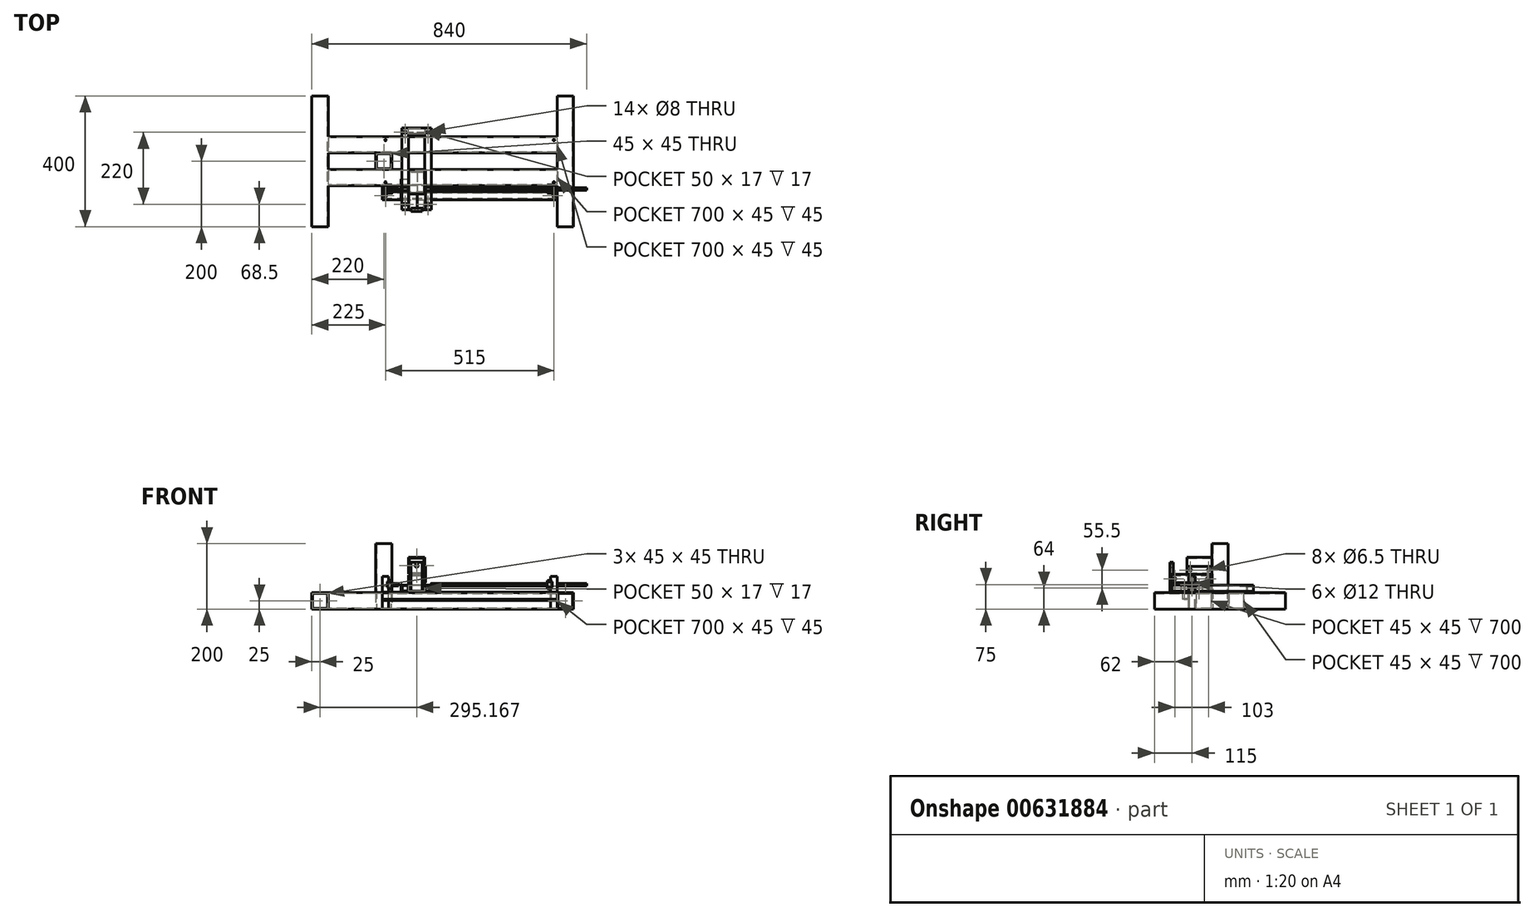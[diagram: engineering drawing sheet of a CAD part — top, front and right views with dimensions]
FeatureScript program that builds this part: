
annotation { "Feature Type Name" : "Feature", "Feature Type Description" : "" }
export const myFeature = defineFeature(function(context is Context, id is Id, definition is map)
    precondition{}
    {
        {
            var Q0;
            Q0=qCreatedBy(makeId("Front.planeOp"),FACE);
            var sketch = newSketch(context, id + "F0", { "sketchPlane" : qUnion([Q0])});
            skLineSegment(sketch, "E0.bottom", {"start": v(-400, -25) * mm, "end": v(-350, -25) * mm});
            skLineSegment(sketch, "E0.top", {"start": v(-400, 25) * mm, "end": v(-350, 25) * mm});
            skLineSegment(sketch, "E0.left", {"start": v(-400, -25) * mm, "end": v(-400, 25) * mm});
            skLineSegment(sketch, "E0.right", {"start": v(-350, -25) * mm, "end": v(-350, 25) * mm});
            skPoint(sketch, "E0.middle", {"position": v(-375, 0) * mm});
            skLineSegment(sketch, "E1.bottom", {"start": v(350, -25) * mm, "end": v(400, -25) * mm});
            skLineSegment(sketch, "E1.top", {"start": v(350, 25) * mm, "end": v(400, 25) * mm});
            skLineSegment(sketch, "E1.left", {"start": v(350, -25) * mm, "end": v(350, 25) * mm});
            skLineSegment(sketch, "E1.right", {"start": v(400, -25) * mm, "end": v(400, 25) * mm});
            skPoint(sketch, "E1.middle", {"position": v(375, 0) * mm});
            skLineSegment(sketch, "E2.bottom", {"start": v(-397.5, -22.5) * mm, "end": v(-352.5, -22.5) * mm});
            skLineSegment(sketch, "E2.top", {"start": v(-397.5, 22.5) * mm, "end": v(-352.5, 22.5) * mm});
            skLineSegment(sketch, "E2.left", {"start": v(-397.5, -22.5) * mm, "end": v(-397.5, 22.5) * mm});
            skLineSegment(sketch, "E2.right", {"start": v(-352.5, -22.5) * mm, "end": v(-352.5, 22.5) * mm});
            skLineSegment(sketch, "E3.bottom", {"start": v(352.5, -22.5) * mm, "end": v(397.5, -22.5) * mm});
            skLineSegment(sketch, "E3.top", {"start": v(352.5, 22.5) * mm, "end": v(397.5, 22.5) * mm});
            skLineSegment(sketch, "E3.left", {"start": v(352.5, -22.5) * mm, "end": v(352.5, 22.5) * mm});
            skLineSegment(sketch, "E3.right", {"start": v(397.5, -22.5) * mm, "end": v(397.5, 22.5) * mm});
            skSolve(sketch);
        }
        {
            var Q0;
            Q0=qSketchRegion(id+"F0",true);
            extrude(context, id + "F1", {"entities" : qUnion([Q0]), "endBound" : BoundingType.SYMMETRIC, "depth" : 400 * mm, "offsetDistance" : 25 * mm});
        }
        {
            var Q0;
            Q0=makeQuery(id+"F1.opExtrude","SWEPT_FACE",FACE,{"disambiguationData":[OSD([sQuery(id+"F0.wireOp",EDGE,"E0.right")])]});
            var sketch = newSketch(context, id + "F2", { "sketchPlane" : qUnion([Q0])});
            skPoint(sketch, "E4.middle", {"position": v(0, 0) * mm});
            skLineSegment(sketch, "E5.bottom", {"start": v(75, -25) * mm, "end": v(25, -25) * mm});
            skLineSegment(sketch, "E5.top", {"start": v(75, 25) * mm, "end": v(25, 25) * mm});
            skLineSegment(sketch, "E5.left", {"start": v(75, -25) * mm, "end": v(75, 25) * mm});
            skLineSegment(sketch, "E5.right", {"start": v(25, -25) * mm, "end": v(25, 25) * mm});
            skPoint(sketch, "E5.middle", {"position": v(50, 0) * mm});
            skLineSegment(sketch, "E6.bottom", {"start": v(-25, -25) * mm, "end": v(-75, -25) * mm});
            skLineSegment(sketch, "E6.top", {"start": v(-25, 25) * mm, "end": v(-75, 25) * mm});
            skLineSegment(sketch, "E6.left", {"start": v(-25, -25) * mm, "end": v(-25, 25) * mm});
            skLineSegment(sketch, "E6.right", {"start": v(-75, -25) * mm, "end": v(-75, 25) * mm});
            skPoint(sketch, "E6.middle", {"position": v(-50, 0) * mm});
            skLineSegment(sketch, "E7.bottom", {"start": v(72.5, 22.5) * mm, "end": v(27.5, 22.5) * mm});
            skLineSegment(sketch, "E7.top", {"start": v(72.5, -22.5) * mm, "end": v(27.5, -22.5) * mm});
            skLineSegment(sketch, "E7.left", {"start": v(72.5, 22.5) * mm, "end": v(72.5, -22.5) * mm});
            skLineSegment(sketch, "E7.right", {"start": v(27.5, 22.5) * mm, "end": v(27.5, -22.5) * mm});
            skLineSegment(sketch, "E8.bottom", {"start": v(-27.5, 22.5) * mm, "end": v(-72.5, 22.5) * mm});
            skLineSegment(sketch, "E8.top", {"start": v(-27.5, -22.5) * mm, "end": v(-72.5, -22.5) * mm});
            skLineSegment(sketch, "E8.left", {"start": v(-27.5, 22.5) * mm, "end": v(-27.5, -22.5) * mm});
            skLineSegment(sketch, "E8.right", {"start": v(-72.5, 22.5) * mm, "end": v(-72.5, -22.5) * mm});
            skSolve(sketch);
        }
        {
            var Q0;
            Q0=qSketchRegion(id+"F2",true);
            extrude(context, id + "F3", {"entities" : qUnion([Q0]), "operationType" : NewBodyOperationType.ADD, "endBound" : BoundingType.UP_TO_NEXT, "depth" : 25 * mm, "offsetDistance" : 25 * mm});
        }
        {
            var Q0;
            Q0=makeQuery(id+"F3.boolean.opBoolean","MERGE",FACE,{"derivedFrom":[makeQuery(id+"F1.opExtrude","SWEPT_FACE",FACE,{"disambiguationData":[OSD([sQuery(id+"F0.wireOp",EDGE,"E0.top")])]}),makeQuery(id+"F1.opExtrude","SWEPT_FACE",FACE,{"disambiguationData":[OSD([sQuery(id+"F0.wireOp",EDGE,"E1.top")])]}),makeQuery(id+"F3.opExtrude","SWEPT_FACE",FACE,{"disambiguationData":[OSD([sQuery(id+"F2.wireOp",EDGE,"E5.top")])]}),makeQuery(id+"F3.opExtrude","SWEPT_FACE",FACE,{"disambiguationData":[OSD([sQuery(id+"F2.wireOp",EDGE,"E6.top")])]})]});
            var sketch = newSketch(context, id + "F4", { "sketchPlane" : qUnion([Q0])});
            skLineSegment(sketch, "E9.bottom", {"start": v(350, -75) * mm, "end": v(330, -75) * mm});
            skLineSegment(sketch, "E9.top", {"start": v(350, -95) * mm, "end": v(330, -95) * mm});
            skLineSegment(sketch, "E9.left", {"start": v(350, -75) * mm, "end": v(350, -95) * mm});
            skLineSegment(sketch, "E9.right", {"start": v(330, -75) * mm, "end": v(330, -95) * mm});
            skLineSegment(sketch, "E10.bottom", {"start": v(-165, -75) * mm, "end": v(-185, -75) * mm});
            skLineSegment(sketch, "E10.top", {"start": v(-165, -95) * mm, "end": v(-185, -95) * mm});
            skLineSegment(sketch, "E10.left", {"start": v(-165, -75) * mm, "end": v(-165, -95) * mm});
            skLineSegment(sketch, "E10.right", {"start": v(-185, -75) * mm, "end": v(-185, -95) * mm});
            skLineSegment(sketch, "E11.bottom", {"start": v(-183.5, -93.5) * mm, "end": v(-166.5, -93.5) * mm});
            skLineSegment(sketch, "E11.top", {"start": v(-183.5, -76.5) * mm, "end": v(-166.5, -76.5) * mm});
            skLineSegment(sketch, "E11.left", {"start": v(-183.5, -93.5) * mm, "end": v(-183.5, -76.5) * mm});
            skLineSegment(sketch, "E11.right", {"start": v(-166.5, -93.5) * mm, "end": v(-166.5, -76.5) * mm});
            skPoint(sketch, "E11.middle", {"position": v(-175, -85) * mm});
            skPoint(sketch, "E11.middle.positionSnap0", {"position": v(-165, -85) * mm});
            skPoint(sketch, "E11.middle.positionSnap1", {"position": v(-175, -95) * mm});
            skPoint(sketch, "E11.centerSnap0", {"position": v(-165, -85) * mm});
            skPoint(sketch, "E11.centerSnap1", {"position": v(-175, -95) * mm});
            skLineSegment(sketch, "E12.bottom", {"start": v(331.5, -93.5) * mm, "end": v(348.5, -93.5) * mm});
            skLineSegment(sketch, "E12.top", {"start": v(331.5, -76.5) * mm, "end": v(348.5, -76.5) * mm});
            skLineSegment(sketch, "E12.left", {"start": v(331.5, -93.5) * mm, "end": v(331.5, -76.5) * mm});
            skLineSegment(sketch, "E12.right", {"start": v(348.5, -93.5) * mm, "end": v(348.5, -76.5) * mm});
            skPoint(sketch, "E12.middle", {"position": v(340, -85) * mm});
            skPoint(sketch, "E12.middle.positionSnap0", {"position": v(330, -85) * mm});
            skPoint(sketch, "E12.middle.positionSnap1", {"position": v(340, -75) * mm});
            skPoint(sketch, "E12.centerSnap0", {"position": v(330, -85) * mm});
            skPoint(sketch, "E12.centerSnap1", {"position": v(340, -75) * mm});
            skSolve(sketch);
        }
        {
            var Q0;
            Q0=qSketchRegion(id+"F4",true);
            extrude(context, id + "F5", {"entities" : qUnion([Q0]), "operationType" : NewBodyOperationType.ADD, "oppositeDirection" : true, "depth" : 50 * mm, "offsetDistance" : 25 * mm});
        }
        {
            var Q0;
            Q0=qSketchRegion(id+"F4",true);
            extrude(context, id + "F6", {"entities" : qUnion([Q0]), "operationType" : NewBodyOperationType.ADD, "depth" : 50 * mm, "offsetDistance" : 25 * mm});
        }
        {
            var Q0;
            {var subQ1=sQuery(id+"F0.wireOp",EDGE,"E1.left");Q0=makeQuery(id+"F3.boolean.opBoolean","SPLIT",FACE,{"disambiguationData":[TD([makeQuery(id+"F3.opExtrude","SWEPT_FACE",FACE,{"disambiguationData":[OSD([sQuery(id+"F2.wireOp",EDGE,"E6.right")])]})])],"derivedFrom":makeQuery(id+"F1.opExtrude","SWEPT_FACE",FACE,{"disambiguationData":[OSD([subQ1])]})});}
            var sketch = newSketch(context, id + "F7", { "sketchPlane" : qUnion([Q0])});
            skLineSegment(sketch, "E13.bottom", {"start": v(95, 25) * mm, "end": v(115, 25) * mm});
            skLineSegment(sketch, "E13.top", {"start": v(95, 5) * mm, "end": v(115, 5) * mm});
            skLineSegment(sketch, "E13.left", {"start": v(95, 25) * mm, "end": v(95, 5) * mm});
            skLineSegment(sketch, "E13.right", {"start": v(115, 25) * mm, "end": v(115, 5) * mm});
            skPoint(sketch, "E13.middle", {"position": v(105, 15) * mm});
            skLineSegment(sketch, "E14.bottom", {"start": v(96.5, 6.5) * mm, "end": v(113.5, 6.5) * mm});
            skLineSegment(sketch, "E14.top", {"start": v(96.5, 23.5) * mm, "end": v(113.5, 23.5) * mm});
            skLineSegment(sketch, "E14.left", {"start": v(96.5, 6.5) * mm, "end": v(96.5, 23.5) * mm});
            skLineSegment(sketch, "E14.right", {"start": v(113.5, 6.5) * mm, "end": v(113.5, 23.5) * mm});
            skSolve(sketch);
        }
        {
            var Q0;
            Q0=qSketchRegion(id+"F7",true);
            extrude(context, id + "F8", {"entities" : qUnion([Q0]), "operationType" : NewBodyOperationType.ADD, "depth" : 535 * mm, "offsetDistance" : 25 * mm});
        }
        {
            var Q0;
            Q0=makeQuery(id+"F6.opExtrude","SWEPT_FACE",FACE,{"disambiguationData":[OSD([sQuery(id+"F4.wireOp",EDGE,"E9.left")])]});
            var sketch = newSketch(context, id + "F9", { "sketchPlane" : qUnion([Q0])});
            skCircle(sketch, "E15", {"center": v(-85, 50) * mm, "radius": 6 * mm});
            skPoint(sketch, "E15.centerSnap0", {"position": v(-85, 75) * mm});
            skSolve(sketch);
        }
        {
            var Q0;
            Q0=qSketchRegion(id+"F9",true);
            extrude(context, id + "F10", {"entities" : qUnion([Q0]), "operationType" : NewBodyOperationType.REMOVE, "endBound" : BoundingType.THROUGH_ALL, "oppositeDirection" : true, "depth" : 242 * mm, "offsetDistance" : 25 * mm});
        }
        {
            var Q0;
            {var subQ0=sQuery(id+"F4.wireOp",EDGE,"E9.right");Q0=makeQuery(id+"F6.boolean.opBoolean","MERGE",FACE,{"derivedFrom":[makeQuery(id+"F5.opExtrude","SWEPT_FACE",FACE,{"disambiguationData":[OSD([subQ0])]}),makeQuery(id+"F6.opExtrude","SWEPT_FACE",FACE,{"disambiguationData":[OSD([subQ0])]})]});}
            var sketch = newSketch(context, id + "F11", { "sketchPlane" : qUnion([Q0])});
            skCircle(sketch, "E16", {"center": v(85, 50) * mm, "radius": 11 * mm});
            skCircle(sketch, "E17", {"center": v(85, 50) * mm, "radius": 13 * mm});
            skSolve(sketch);
        }
        {
            var Q0;
            Q0=qSketchRegion(id+"F11",true);
            extrude(context, id + "F12", {"entities" : qUnion([Q0]), "operationType" : NewBodyOperationType.ADD, "depth" : 10 * mm, "offsetDistance" : 25 * mm});
        }
        {
            var Q0;
            Q0=qSketchRegion(id+"F11",true);
            extrude(context, id + "F13", {"entities" : qUnion([Q0]), "operationType" : NewBodyOperationType.ADD, "oppositeDirection" : true, "depth" : 5 * mm, "offsetDistance" : 25 * mm});
        }
        {
            var Q0;
            {var subQ0=sQuery(id+"F4.wireOp",EDGE,"E10.left");Q0=makeQuery(id+"F6.boolean.opBoolean","MERGE",FACE,{"derivedFrom":[makeQuery(id+"F5.opExtrude","SWEPT_FACE",FACE,{"disambiguationData":[OSD([subQ0])]}),makeQuery(id+"F6.opExtrude","SWEPT_FACE",FACE,{"disambiguationData":[OSD([subQ0])]})]});}
            var sketch = newSketch(context, id + "F14", { "sketchPlane" : qUnion([Q0])});
            skCircle(sketch, "E18", {"center": v(-85, 50) * mm, "radius": 11 * mm});
            skCircle(sketch, "E19", {"center": v(-85, 50) * mm, "radius": 13 * mm});
            skSolve(sketch);
        }
        {
            var Q0;
            Q0=qSketchRegion(id+"F14",true);
            extrude(context, id + "F15", {"entities" : qUnion([Q0]), "operationType" : NewBodyOperationType.ADD, "depth" : 10 * mm, "offsetDistance" : 25 * mm});
        }
        {
            var Q0;
            Q0=qSketchRegion(id+"F14",true);
            extrude(context, id + "F16", {"entities" : qUnion([Q0]), "operationType" : NewBodyOperationType.ADD, "oppositeDirection" : true, "depth" : 5 * mm, "offsetDistance" : 25 * mm});
        }
        {
            var Q0;
            {var subQ0=sQuery(id+"F4.wireOp",EDGE,"E10.left");var subQ1=sQuery(id+"F14.wireOp",EDGE,"E19");Q0=makeQuery(id+"F15.boolean.opBoolean","SPLIT",EDGE,{"disambiguationData":[topologyDisambiguationEdgeConnected([makeQuery(id+"F5.opExtrude","SWEPT_FACE",FACE,{"disambiguationData":[OSD([subQ0])]}),makeQuery(id+"F6.opExtrude","SWEPT_FACE",FACE,{"disambiguationData":[OSD([subQ0])]}),makeQuery(id+"F15.opExtrude","SWEPT_FACE",FACE,{"disambiguationData":[OSD([subQ1])]})]),OD(1.0)],"derivedFrom":makeQuery(id+"F15.opExtrude","CAP_EDGE",EDGE,{"disambiguationData":[OSD([subQ1])],"isStart":true})});}
            var Q1;
            {var subQ0=sQuery(id+"F4.wireOp",EDGE,"E10.left");var subQ1=sQuery(id+"F14.wireOp",EDGE,"E19");Q1=makeQuery(id+"F15.boolean.opBoolean","SPLIT",EDGE,{"disambiguationData":[topologyDisambiguationEdgeConnected([makeQuery(id+"F5.opExtrude","SWEPT_FACE",FACE,{"disambiguationData":[OSD([subQ0])]}),makeQuery(id+"F6.opExtrude","SWEPT_FACE",FACE,{"disambiguationData":[OSD([subQ0])]}),makeQuery(id+"F15.opExtrude","SWEPT_FACE",FACE,{"disambiguationData":[OSD([subQ1])]})]),OD(0.0)],"derivedFrom":makeQuery(id+"F15.opExtrude","CAP_EDGE",EDGE,{"disambiguationData":[OSD([subQ1])],"isStart":true})});}
            var Q2;
            {var subQ0=sQuery(id+"F4.wireOp",EDGE,"E9.right");var subQ1=sQuery(id+"F11.wireOp",EDGE,"E17");Q2=makeQuery(id+"F12.boolean.opBoolean","SPLIT",EDGE,{"disambiguationData":[topologyDisambiguationEdgeConnected([makeQuery(id+"F5.opExtrude","SWEPT_FACE",FACE,{"disambiguationData":[OSD([subQ0])]}),makeQuery(id+"F6.opExtrude","SWEPT_FACE",FACE,{"disambiguationData":[OSD([subQ0])]}),makeQuery(id+"F12.opExtrude","SWEPT_FACE",FACE,{"disambiguationData":[OSD([subQ1])]})]),OD(1.0)],"derivedFrom":makeQuery(id+"F12.opExtrude","CAP_EDGE",EDGE,{"disambiguationData":[OSD([subQ1])],"isStart":true})});}
            var Q3;
            {var subQ0=sQuery(id+"F4.wireOp",EDGE,"E9.right");var subQ1=sQuery(id+"F11.wireOp",EDGE,"E17");Q3=makeQuery(id+"F12.boolean.opBoolean","SPLIT",EDGE,{"disambiguationData":[topologyDisambiguationEdgeConnected([makeQuery(id+"F5.opExtrude","SWEPT_FACE",FACE,{"disambiguationData":[OSD([subQ0])]}),makeQuery(id+"F6.opExtrude","SWEPT_FACE",FACE,{"disambiguationData":[OSD([subQ0])]}),makeQuery(id+"F12.opExtrude","SWEPT_FACE",FACE,{"disambiguationData":[OSD([subQ1])]})]),OD(0.0)],"derivedFrom":makeQuery(id+"F12.opExtrude","CAP_EDGE",EDGE,{"disambiguationData":[OSD([subQ1])],"isStart":true})});}
            chamfer(context, id + "F17", {"entities" : qUnion([Q0, Q1, Q2, Q3]), "width" : 5 * mm, "tangentPropagation" : true});
        }
        {
            var Q0;
            Q0=makeQuery(id+"F8.boolean.opBoolean","MERGE",FACE,{"derivedFrom":[makeQuery(id+"F5.boolean.opBoolean","MERGE",FACE,{"derivedFrom":[makeQuery(id+"F3.boolean.opBoolean","MERGE",FACE,{"derivedFrom":[makeQuery(id+"F1.opExtrude","SWEPT_FACE",FACE,{"disambiguationData":[OSD([sQuery(id+"F0.wireOp",EDGE,"E0.top")])]}),makeQuery(id+"F1.opExtrude","SWEPT_FACE",FACE,{"disambiguationData":[OSD([sQuery(id+"F0.wireOp",EDGE,"E1.top")])]}),makeQuery(id+"F3.opExtrude","SWEPT_FACE",FACE,{"disambiguationData":[OSD([sQuery(id+"F2.wireOp",EDGE,"E5.top")])]}),makeQuery(id+"F3.opExtrude","SWEPT_FACE",FACE,{"disambiguationData":[OSD([sQuery(id+"F2.wireOp",EDGE,"E6.top")])]})]}),makeQuery(id+"F5.opExtrude","CAP_FACE",FACE,{"disambiguationData":[OSD([sQuery(id+"F4.wireOp",EDGE,"E9.bottom"),sQuery(id+"F4.wireOp",EDGE,"E9.top"),sQuery(id+"F4.wireOp",EDGE,"E9.left"),sQuery(id+"F4.wireOp",EDGE,"E9.right"),sQuery(id+"F4.wireOp",EDGE,"E12.bottom"),sQuery(id+"F4.wireOp",EDGE,"E12.top"),sQuery(id+"F4.wireOp",EDGE,"E12.left"),sQuery(id+"F4.wireOp",EDGE,"E12.right")])],"isStart":true}),makeQuery(id+"F5.opExtrude","CAP_FACE",FACE,{"disambiguationData":[OSD([sQuery(id+"F4.wireOp",EDGE,"E10.bottom"),sQuery(id+"F4.wireOp",EDGE,"E10.top"),sQuery(id+"F4.wireOp",EDGE,"E10.left"),sQuery(id+"F4.wireOp",EDGE,"E10.right"),sQuery(id+"F4.wireOp",EDGE,"E11.bottom"),sQuery(id+"F4.wireOp",EDGE,"E11.top"),sQuery(id+"F4.wireOp",EDGE,"E11.left"),sQuery(id+"F4.wireOp",EDGE,"E11.right")])],"isStart":true})]}),makeQuery(id+"F8.opExtrude","SWEPT_FACE",FACE,{"disambiguationData":[OSD([sQuery(id+"F7.wireOp",EDGE,"E13.bottom")])]})]});
            var sketch = newSketch(context, id + "F18", { "sketchPlane" : qUnion([Q0])});
            skCircle(sketch, "E20", {"center": v(-175, -65) * mm, "radius": 2.5 * mm});
            skCircle(sketch, "E21", {"center": v(-175, 65) * mm, "radius": 2.5 * mm});
            skCircle(sketch, "E22", {"center": v(-175, -105) * mm, "radius": 2.5 * mm});
            skCircle(sketch, "E23", {"center": v(340, -105) * mm, "radius": 2.5 * mm});
            skCircle(sketch, "E24", {"center": v(340, -65) * mm, "radius": 2.5 * mm});
            skCircle(sketch, "E25", {"center": v(340, 65) * mm, "radius": 2.5 * mm});
            skSolve(sketch);
        }
        {
            var Q0;
            Q0=qSketchRegion(id+"F18",true);
            extrude(context, id + "F19", {"entities" : qUnion([Q0]), "operationType" : NewBodyOperationType.REMOVE, "oppositeDirection" : true, "depth" : 10 * mm, "offsetDistance" : 25 * mm});
        }
        {
            var Q0;
            Q0=makeQuery(id+"F6.opExtrude","SWEPT_FACE",FACE,{"disambiguationData":[OSD([sQuery(id+"F4.wireOp",EDGE,"E9.left")])]});
            var sketch = newSketch(context, id + "F20", { "sketchPlane" : qUnion([Q0])});
            skLineSegment(sketch, "E26", {"start": v(-118, 25) * mm, "end": v(-95, 25) * mm});
            skLineSegment(sketch, "E27", {"start": v(-95, 25) * mm, "end": v(-95, 2) * mm});
            skLineSegment(sketch, "E28", {"start": v(-95, 2) * mm, "end": v(-93, 2) * mm});
            skLineSegment(sketch, "E29", {"start": v(-93, 2) * mm, "end": v(-93, 27) * mm});
            skLineSegment(sketch, "E30", {"start": v(-93, 27) * mm, "end": v(-118, 27) * mm});
            skLineSegment(sketch, "E31", {"start": v(-118, 27) * mm, "end": v(-118, 25) * mm});
            skSolve(sketch);
        }
        {
            var Q0;
            Q0 = qSketchRegion(id + "F20", true);
            extrude(context, id + "F21", {"entities" : qUnion([Q0]), "oppositeDirection" : true, "depth" : 535 * mm, "offsetDistance" : 25 * mm});
        }
        {
            var Q0;
            Q0=makeQuery(id+"F21.opExtrude","SWEPT_FACE",FACE,{"disambiguationData":[OSD([sQuery(id+"F20.wireOp",EDGE,"E30")])]});
            var sketch = newSketch(context, id + "F22", { "sketchPlane" : qUnion([Q0])});
            skLineSegment(sketch, "E32.bottom", {"start": v(-185, -93) * mm, "end": v(-165, -93) * mm});
            skLineSegment(sketch, "E32.top", {"start": v(-185, -95) * mm, "end": v(-165, -95) * mm});
            skLineSegment(sketch, "E32.left", {"start": v(-185, -93) * mm, "end": v(-185, -95) * mm});
            skLineSegment(sketch, "E32.right", {"start": v(-165, -93) * mm, "end": v(-165, -95) * mm});
            skLineSegment(sketch, "E33.bottom", {"start": v(350, -93) * mm, "end": v(330, -93) * mm});
            skLineSegment(sketch, "E33.top", {"start": v(350, -95) * mm, "end": v(330, -95) * mm});
            skLineSegment(sketch, "E33.left", {"start": v(350, -93) * mm, "end": v(350, -95) * mm});
            skLineSegment(sketch, "E33.right", {"start": v(330, -93) * mm, "end": v(330, -95) * mm});
            skCircle(sketch, "E34", {"center": v(-175, -105) * mm, "radius": 4 * mm});
            skCircle(sketch, "E35", {"center": v(340, -105) * mm, "radius": 4 * mm});
            skSolve(sketch);
        }
        {
            var Q0;
            Q0 = qSketchRegion(id + "F22", true);
            extrude(context, id + "F23", {"entities" : qUnion([Q0]), "operationType" : NewBodyOperationType.REMOVE, "oppositeDirection" : true, "depth" : 26 * mm, "offsetDistance" : 25 * mm});
        }
        {
            var Q0;
            Q0=makeQuery(id+"F6.opExtrude","SWEPT_FACE",FACE,{"disambiguationData":[OSD([sQuery(id+"F4.wireOp",EDGE,"E9.left")])]});
            var sketch = newSketch(context, id + "F24", { "sketchPlane" : qUnion([Q0])});
            skCircle(sketch, "E36", {"center": v(-85, 50) * mm, "radius": 3.8 * mm});
            skSolve(sketch);
        }
        {
            var Q0;
            Q0 = qSketchRegion(id + "F24", true);
            extrude(context, id + "F25", {"entities" : qUnion([Q0]), "oppositeDirection" : true, "depth" : 535 * mm, "offsetDistance" : 25 * mm, "hasSecondDirection" : true, "secondDirectionOppositeDirection" : false, "secondDirectionDepth" : 90 * mm});
        }
        {
            var Q0;
            Q0=makeQuery(id+"F21.opExtrude","SWEPT_FACE",FACE,{"disambiguationData":[OSD([sQuery(id+"F20.wireOp",EDGE,"E31")])]});
            var sketch = newSketch(context, id + "F26", { "sketchPlane" : qUnion([Q0])});
            skLineSegment(sketch, "E37", {"start": v(-126.83, 27) * mm, "end": v(-126.83, 52) * mm});
            skLineSegment(sketch, "E38", {"start": v(-126.83, 52) * mm, "end": v(-124.83, 52) * mm});
            skLineSegment(sketch, "E39", {"start": v(-124.83, 52) * mm, "end": v(-124.83, 29) * mm});
            skLineSegment(sketch, "E40", {"start": v(-124.83, 29) * mm, "end": v(-101.83, 29) * mm});
            skLineSegment(sketch, "E41", {"start": v(-101.83, 29) * mm, "end": v(-101.83, 27) * mm});
            skLineSegment(sketch, "E42", {"start": v(-101.83, 27) * mm, "end": v(-126.83, 27) * mm});
            skSolve(sketch);
        }
        {
            var Q0;
            Q0 = qSketchRegion(id + "F26", true);
            extrude(context, id + "F27", {"entities" : qUnion([Q0]), "oppositeDirection" : true, "depth" : 64 * mm, "offsetDistance" : 25 * mm});
        }
        {
            var Q0;
            Q0=makeQuery(id+"F27.opExtrude","SWEPT_FACE",FACE,{"disambiguationData":[OSD([sQuery(id+"F26.wireOp",EDGE,"E37")])]});
            var sketch = newSketch(context, id + "F28", { "sketchPlane" : qUnion([Q0])});
            skArc(sketch, "E43", {"start": v(79, 50) * mm, "mid": v(85, 44) * mm, "end": v(91, 50) * mm});
            skLineSegment(sketch, "E44", {"start": v(79, 50) * mm, "end": v(79, 58) * mm});
            skLineSegment(sketch, "E45", {"start": v(79, 58) * mm, "end": v(91, 58) * mm});
            skLineSegment(sketch, "E46", {"start": v(91, 58) * mm, "end": v(91, 50) * mm});
            skCircle(sketch, "E47", {"center": v(64, 39) * mm, "radius": 3.25 * mm});
            skCircle(sketch, "E48", {"center": v(108, 39) * mm, "radius": 3.25 * mm});
            skSolve(sketch);
        }
        {
            var Q0;
            Q0 = qSketchRegion(id + "F28", true);
            extrude(context, id + "F29", {"entities" : qUnion([Q0]), "operationType" : NewBodyOperationType.REMOVE, "oppositeDirection" : true, "depth" : 60.5 * mm, "offsetDistance" : 25 * mm});
        }
        {
            var Q0;
            Q0=makeQuery(id+"F27.opExtrude","CAP_FACE",FACE,{"disambiguationData":[OSD([sQuery(id+"F26.wireOp",EDGE,"E37"),sQuery(id+"F26.wireOp",EDGE,"E38"),sQuery(id+"F26.wireOp",EDGE,"E39"),sQuery(id+"F26.wireOp",EDGE,"E40"),sQuery(id+"F26.wireOp",EDGE,"E41"),sQuery(id+"F26.wireOp",EDGE,"E42")])],"isStart":true});
            var sketch = newSketch(context, id + "F30", { "sketchPlane" : qUnion([Q0])});
            skLineSegment(sketch, "E49.bottom", {"start": v(-124.83, 29) * mm, "end": v(-104.83, 29) * mm});
            skLineSegment(sketch, "E49.top", {"start": v(-124.83, 49) * mm, "end": v(-104.83, 49) * mm});
            skLineSegment(sketch, "E49.left", {"start": v(-124.83, 29) * mm, "end": v(-124.83, 49) * mm});
            skLineSegment(sketch, "E49.right", {"start": v(-104.83, 29) * mm, "end": v(-104.83, 49) * mm});
            skLineSegment(sketch, "E50.bottom", {"start": v(-104.83, 29) * mm, "end": v(-54.83, 29) * mm});
            skLineSegment(sketch, "E50.top", {"start": v(-104.83, 79) * mm, "end": v(-54.83, 79) * mm});
            skLineSegment(sketch, "E50.left", {"start": v(-104.83, 29) * mm, "end": v(-104.83, 79) * mm});
            skLineSegment(sketch, "E50.right", {"start": v(-54.83, 29) * mm, "end": v(-54.83, 79) * mm});
            skLineSegment(sketch, "E51.bottom", {"start": v(-54.83, 29) * mm, "end": v(-34.83, 29) * mm});
            skLineSegment(sketch, "E51.top", {"start": v(-54.83, 49) * mm, "end": v(-34.83, 49) * mm});
            skLineSegment(sketch, "E51.left", {"start": v(-54.83, 29) * mm, "end": v(-54.83, 49) * mm});
            skLineSegment(sketch, "E51.right", {"start": v(-34.83, 29) * mm, "end": v(-34.83, 49) * mm});
            skLineSegment(sketch, "E52.bottom", {"start": v(-102.33, 31.5) * mm, "end": v(-57.33, 31.5) * mm});
            skLineSegment(sketch, "E52.top", {"start": v(-102.33, 76.5) * mm, "end": v(-57.33, 76.5) * mm});
            skLineSegment(sketch, "E52.left", {"start": v(-102.33, 31.5) * mm, "end": v(-102.33, 76.5) * mm});
            skLineSegment(sketch, "E52.right", {"start": v(-57.33, 31.5) * mm, "end": v(-57.33, 76.5) * mm});
            skPoint(sketch, "E52.middle", {"position": v(-79.83, 54) * mm});
            skPoint(sketch, "E52.middle.positionSnap0", {"position": v(-79.83, 79) * mm});
            skPoint(sketch, "E52.middle.positionSnap1", {"position": v(-104.83, 54) * mm});
            skPoint(sketch, "E52.centerSnap0", {"position": v(-79.83, 79) * mm});
            skPoint(sketch, "E52.centerSnap1", {"position": v(-104.83, 54) * mm});
            skLineSegment(sketch, "E53.bottom", {"start": v(-123.33, 30.5) * mm, "end": v(-106.33, 30.5) * mm});
            skLineSegment(sketch, "E53.top", {"start": v(-123.33, 47.5) * mm, "end": v(-106.33, 47.5) * mm});
            skLineSegment(sketch, "E53.left", {"start": v(-123.33, 30.5) * mm, "end": v(-123.33, 47.5) * mm});
            skLineSegment(sketch, "E53.right", {"start": v(-106.33, 30.5) * mm, "end": v(-106.33, 47.5) * mm});
            skPoint(sketch, "E53.middle", {"position": v(-114.83, 39) * mm});
            skPoint(sketch, "E53.middle.positionSnap0", {"position": v(-104.83, 39) * mm});
            skPoint(sketch, "E53.middle.positionSnap1", {"position": v(-114.83, 49) * mm});
            skPoint(sketch, "E53.centerSnap0", {"position": v(-104.83, 39) * mm});
            skPoint(sketch, "E53.centerSnap1", {"position": v(-114.83, 49) * mm});
            skLineSegment(sketch, "E54.bottom", {"start": v(-53.33, 30.5) * mm, "end": v(-36.33, 30.5) * mm});
            skLineSegment(sketch, "E54.top", {"start": v(-53.33, 47.5) * mm, "end": v(-36.33, 47.5) * mm});
            skLineSegment(sketch, "E54.left", {"start": v(-53.33, 30.5) * mm, "end": v(-53.33, 47.5) * mm});
            skLineSegment(sketch, "E54.right", {"start": v(-36.33, 30.5) * mm, "end": v(-36.33, 47.5) * mm});
            skPoint(sketch, "E54.middle", {"position": v(-44.83, 39) * mm});
            skPoint(sketch, "E54.middle.positionSnap0", {"position": v(-44.83, 49) * mm});
            skPoint(sketch, "E54.centerSnap0", {"position": v(-44.83, 49) * mm});
            skSolve(sketch);
        }
        {
            var Q0;
            Q0 = qSketchRegion(id + "F30", true);
            extrude(context, id + "F31", {"entities" : qUnion([Q0]), "oppositeDirection" : true, "depth" : 90 * mm, "offsetDistance" : 25 * mm, "hasSecondDirection" : true, "secondDirectionOppositeDirection" : false, "secondDirectionDepth" : 30 * mm});
        }
        {
            var Q0;
            Q0=makeQuery(id+"F31.opExtrude","SWEPT_FACE",FACE,{"disambiguationData":[OSD([sQuery(id+"F30.wireOp",EDGE,"E51.right")])]});
            var sketch = newSketch(context, id + "F32", { "sketchPlane" : qUnion([Q0])});
            skCircle(sketch, "E55", {"center": v(-85, 50) * mm, "radius": 6 * mm});
            skCircle(sketch, "E56", {"center": v(-138, 67.5) * mm, "radius": 3.25 * mm});
            skCircle(sketch, "E57", {"center": v(-38, 67.5) * mm, "radius": 3.25 * mm});
            skSolve(sketch);
        }
        {
            var Q0;
            Q0 = qSketchRegion(id + "F32", true);
            extrude(context, id + "F33", {"entities" : qUnion([Q0]), "operationType" : NewBodyOperationType.REMOVE, "oppositeDirection" : true, "depth" : 100.4 * mm, "offsetDistance" : 25 * mm});
        }
        {
            var Q0;
            Q0=makeQuery(id+"F31.opExtrude","CAP_FACE",FACE,{"disambiguationData":[OSD([sQuery(id+"F30.wireOp",EDGE,"E49.bottom"),sQuery(id+"F30.wireOp",EDGE,"E49.top"),sQuery(id+"F30.wireOp",EDGE,"E49.left"),sQuery(id+"F30.wireOp",EDGE,"E50.bottom"),sQuery(id+"F30.wireOp",EDGE,"E50.top"),sQuery(id+"F30.wireOp",EDGE,"E50.left"),sQuery(id+"F30.wireOp",EDGE,"E50.right"),sQuery(id+"F30.wireOp",EDGE,"E51.bottom"),sQuery(id+"F30.wireOp",EDGE,"E51.top"),sQuery(id+"F30.wireOp",EDGE,"E51.right"),sQuery(id+"F30.wireOp",EDGE,"E52.bottom"),sQuery(id+"F30.wireOp",EDGE,"E52.top"),sQuery(id+"F30.wireOp",EDGE,"E52.left"),sQuery(id+"F30.wireOp",EDGE,"E52.right"),sQuery(id+"F30.wireOp",EDGE,"E53.bottom"),sQuery(id+"F30.wireOp",EDGE,"E53.top"),sQuery(id+"F30.wireOp",EDGE,"E53.left"),sQuery(id+"F30.wireOp",EDGE,"E53.right"),sQuery(id+"F30.wireOp",EDGE,"E54.bottom"),sQuery(id+"F30.wireOp",EDGE,"E54.top"),sQuery(id+"F30.wireOp",EDGE,"E54.left"),sQuery(id+"F30.wireOp",EDGE,"E54.right")])],"isStart":false});
            var sketch = newSketch(context, id + "F34", { "sketchPlane" : qUnion([Q0])});
            skLineSegment(sketch, "E58.bottom", {"start": v(34.83, 49) * mm, "end": v(54.83, 49) * mm});
            skLineSegment(sketch, "E58.top", {"start": v(34.83, 29) * mm, "end": v(54.83, 29) * mm});
            skLineSegment(sketch, "E58.left", {"start": v(34.83, 49) * mm, "end": v(34.83, 29) * mm});
            skLineSegment(sketch, "E58.right", {"start": v(54.83, 49) * mm, "end": v(54.83, 29) * mm});
            skPoint(sketch, "E58.middle", {"position": v(44.83, 39) * mm});
            skPoint(sketch, "E58.middle.positionSnap0", {"position": v(44.83, 47.5) * mm});
            skPoint(sketch, "E58.middle.positionSnap1", {"position": v(36.33, 39) * mm});
            skPoint(sketch, "E58.centerSnap0", {"position": v(44.83, 47.5) * mm});
            skPoint(sketch, "E58.centerSnap1", {"position": v(36.33, 39) * mm});
            skLineSegment(sketch, "E59.bottom", {"start": v(104.83, 49) * mm, "end": v(124.83, 49) * mm});
            skLineSegment(sketch, "E59.top", {"start": v(104.83, 29) * mm, "end": v(124.83, 29) * mm});
            skLineSegment(sketch, "E59.left", {"start": v(104.83, 49) * mm, "end": v(104.83, 29) * mm});
            skLineSegment(sketch, "E59.right", {"start": v(124.83, 49) * mm, "end": v(124.83, 29) * mm});
            skPoint(sketch, "E59.middle", {"position": v(114.83, 39) * mm});
            skPoint(sketch, "E59.middle.positionSnap0", {"position": v(114.83, 47.5) * mm});
            skPoint(sketch, "E59.middle.positionSnap1", {"position": v(106.33, 39) * mm});
            skPoint(sketch, "E59.centerSnap0", {"position": v(114.83, 47.5) * mm});
            skPoint(sketch, "E59.centerSnap1", {"position": v(106.33, 39) * mm});
            skLineSegment(sketch, "E60.bottom", {"start": v(106.33, 47.5) * mm, "end": v(123.33, 47.5) * mm});
            skLineSegment(sketch, "E60.top", {"start": v(106.33, 30.5) * mm, "end": v(123.33, 30.5) * mm});
            skLineSegment(sketch, "E60.left", {"start": v(106.33, 47.5) * mm, "end": v(106.33, 30.5) * mm});
            skLineSegment(sketch, "E60.right", {"start": v(123.33, 47.5) * mm, "end": v(123.33, 30.5) * mm});
            skLineSegment(sketch, "E61.bottom", {"start": v(36.33, 47.5) * mm, "end": v(53.33, 47.5) * mm});
            skLineSegment(sketch, "E61.top", {"start": v(36.33, 30.5) * mm, "end": v(53.33, 30.5) * mm});
            skLineSegment(sketch, "E61.left", {"start": v(36.33, 47.5) * mm, "end": v(36.33, 30.5) * mm});
            skLineSegment(sketch, "E61.right", {"start": v(53.33, 47.5) * mm, "end": v(53.33, 30.5) * mm});
            skSolve(sketch);
        }
        {
            var Q0;
            Q0 = qSketchRegion(id + "F34", true);
            extrude(context, id + "F35", {"entities" : qUnion([Q0]), "operationType" : NewBodyOperationType.ADD, "depth" : 130 * mm, "offsetDistance" : 25 * mm});
        }
        {
            var Q0;
            Q0=makeQuery(id+"F31.opExtrude","SWEPT_FACE",FACE,{"disambiguationData":[OSD([sQuery(id+"F30.wireOp",EDGE,"E50.top")])]});
            var sketch = newSketch(context, id + "F36", { "sketchPlane" : qUnion([Q0])});
            skLineSegment(sketch, "E62.bottom", {"start": v(-97.33, -148) * mm, "end": v(-62.33, -148) * mm});
            skLineSegment(sketch, "E62.top", {"start": v(-97.33, -143) * mm, "end": v(-62.33, -143) * mm});
            skLineSegment(sketch, "E62.left", {"start": v(-97.33, -148) * mm, "end": v(-97.33, -143) * mm});
            skLineSegment(sketch, "E62.right", {"start": v(-62.33, -148) * mm, "end": v(-62.33, -143) * mm});
            skCircle(sketch, "E63", {"center": v(-114.83, -131.5) * mm, "radius": 4 * mm});
            skCircle(sketch, "E64", {"center": v(-44.83, -131.5) * mm, "radius": 4 * mm});
            skCircle(sketch, "E65", {"center": v(-44.83, 88.5) * mm, "radius": 4 * mm});
            skCircle(sketch, "E66", {"center": v(-114.83, 88.5) * mm, "radius": 4 * mm});
            skLineSegment(sketch, "E67", {"start": v(-97.33, -28) * mm, "end": v(-97.33, -33) * mm});
            skLineSegment(sketch, "E68", {"start": v(-97.33, -33) * mm, "end": v(-62.33, -33) * mm});
            skLineSegment(sketch, "E69", {"start": v(-62.33, -33) * mm, "end": v(-62.33, -28) * mm});
            skSolve(sketch);
        }
        {
            var Q0;
            Q0=makeQuery(id+"F35.opExtrude","SWEPT_FACE",FACE,{"disambiguationData":[OSD([sQuery(id+"F34.wireOp",EDGE,"E59.left")])]});
            var sketch = newSketch(context, id + "F37", { "sketchPlane" : qUnion([Q0])});
            skLineSegment(sketch, "E70.bottom", {"start": v(102, 49) * mm, "end": v(82, 49) * mm});
            skLineSegment(sketch, "E70.top", {"start": v(102, 29) * mm, "end": v(82, 29) * mm});
            skLineSegment(sketch, "E70.left", {"start": v(102, 49) * mm, "end": v(102, 29) * mm});
            skLineSegment(sketch, "E70.right", {"start": v(82, 49) * mm, "end": v(82, 29) * mm});
            skLineSegment(sketch, "E71.bottom", {"start": v(83.5, 30.5) * mm, "end": v(100.5, 30.5) * mm});
            skLineSegment(sketch, "E71.top", {"start": v(83.5, 47.5) * mm, "end": v(100.5, 47.5) * mm});
            skLineSegment(sketch, "E71.left", {"start": v(83.5, 30.5) * mm, "end": v(83.5, 47.5) * mm});
            skLineSegment(sketch, "E71.right", {"start": v(100.5, 30.5) * mm, "end": v(100.5, 47.5) * mm});
            skPoint(sketch, "E71.middle", {"position": v(92, 39) * mm});
            skPoint(sketch, "E71.middle.positionSnap0", {"position": v(92, 49) * mm});
            skPoint(sketch, "E71.middle.positionSnap1", {"position": v(82, 39) * mm});
            skPoint(sketch, "E71.centerSnap0", {"position": v(92, 49) * mm});
            skPoint(sketch, "E71.centerSnap1", {"position": v(82, 39) * mm});
            skSolve(sketch);
        }
        {
            var Q0;
            Q0 = qSketchRegion(id + "F37", true);
            extrude(context, id + "F38", {"entities" : qUnion([Q0]), "operationType" : NewBodyOperationType.ADD, "endBound" : BoundingType.UP_TO_NEXT, "depth" : 46 * mm, "offsetDistance" : 25 * mm});
        }
        {
            var Q0;
            Q0 = qSketchRegion(id + "F36", true);
            var Q1;
            {var subQ0=sQuery(id+"F36.wireOp",EDGE,"E67");Q1=makeQuery(id+"F36.imprint","IMPRINT",FACE,{"disambiguationData":[TD([[makeQuery(id+"F36.imprint","IMPRINT",EDGE,{"derivedFrom":subQ0}),1.0]])]});}
            extrude(context, id + "F39", {"entities" : qUnion([Q0, Q1]), "operationType" : NewBodyOperationType.REMOVE, "oppositeDirection" : true, "depth" : 87 * mm, "offsetDistance" : 25 * mm});
        }
        {
            var Q0;
            Q0=makeQuery(id+"F5.boolean.opBoolean","MERGE",FACE,{"derivedFrom":[makeQuery(id+"F3.boolean.opBoolean","MERGE",FACE,{"derivedFrom":[makeQuery(id+"F1.opExtrude","SWEPT_FACE",FACE,{"disambiguationData":[OSD([sQuery(id+"F0.wireOp",EDGE,"E0.bottom")])]}),makeQuery(id+"F1.opExtrude","SWEPT_FACE",FACE,{"disambiguationData":[OSD([sQuery(id+"F0.wireOp",EDGE,"E1.bottom")])]}),makeQuery(id+"F3.opExtrude","SWEPT_FACE",FACE,{"disambiguationData":[OSD([sQuery(id+"F2.wireOp",EDGE,"E5.bottom")])]}),makeQuery(id+"F3.opExtrude","SWEPT_FACE",FACE,{"disambiguationData":[OSD([sQuery(id+"F2.wireOp",EDGE,"E6.bottom")])]})]}),makeQuery(id+"F5.opExtrude","CAP_FACE",FACE,{"disambiguationData":[OSD([sQuery(id+"F4.wireOp",EDGE,"E9.bottom"),sQuery(id+"F4.wireOp",EDGE,"E9.top"),sQuery(id+"F4.wireOp",EDGE,"E9.left"),sQuery(id+"F4.wireOp",EDGE,"E9.right"),sQuery(id+"F4.wireOp",EDGE,"E12.bottom"),sQuery(id+"F4.wireOp",EDGE,"E12.top"),sQuery(id+"F4.wireOp",EDGE,"E12.left"),sQuery(id+"F4.wireOp",EDGE,"E12.right")])],"isStart":false}),makeQuery(id+"F5.opExtrude","CAP_FACE",FACE,{"disambiguationData":[OSD([sQuery(id+"F4.wireOp",EDGE,"E10.bottom"),sQuery(id+"F4.wireOp",EDGE,"E10.top"),sQuery(id+"F4.wireOp",EDGE,"E10.left"),sQuery(id+"F4.wireOp",EDGE,"E10.right"),sQuery(id+"F4.wireOp",EDGE,"E11.bottom"),sQuery(id+"F4.wireOp",EDGE,"E11.top"),sQuery(id+"F4.wireOp",EDGE,"E11.left"),sQuery(id+"F4.wireOp",EDGE,"E11.right")])],"isStart":false})]});
            var sketch = newSketch(context, id + "F40", { "sketchPlane" : qUnion([Q0])});
            skLineSegment(sketch, "E72.bottom", {"start": v(-155, 25) * mm, "end": v(-205, 25) * mm});
            skLineSegment(sketch, "E72.top", {"start": v(-155, -25) * mm, "end": v(-205, -25) * mm});
            skLineSegment(sketch, "E72.left", {"start": v(-155, 25) * mm, "end": v(-155, -25) * mm});
            skLineSegment(sketch, "E72.right", {"start": v(-205, 25) * mm, "end": v(-205, -25) * mm});
            skLineSegment(sketch, "E73.bottom", {"start": v(-202.5, 22.5) * mm, "end": v(-157.5, 22.5) * mm});
            skLineSegment(sketch, "E73.top", {"start": v(-202.5, -22.5) * mm, "end": v(-157.5, -22.5) * mm});
            skLineSegment(sketch, "E73.left", {"start": v(-202.5, 22.5) * mm, "end": v(-202.5, -22.5) * mm});
            skLineSegment(sketch, "E73.right", {"start": v(-157.5, 22.5) * mm, "end": v(-157.5, -22.5) * mm});
            skPoint(sketch, "E73.middle", {"position": v(-180, 0) * mm});
            skPoint(sketch, "E73.middle.positionSnap0", {"position": v(-180, 25) * mm});
            skPoint(sketch, "E73.centerSnap0", {"position": v(-180, 25) * mm});
            skSolve(sketch);
        }
        {
            var Q0;
            Q0 = qSketchRegion(id + "F40", true);
            extrude(context, id + "F41", {"entities" : qUnion([Q0]), "operationType" : NewBodyOperationType.ADD, "oppositeDirection" : true, "depth" : 200 * mm, "offsetDistance" : 25 * mm});
        }
        {
            var Q0;
            Q0=makeQuery(id+"F41.opExtrude","SWEPT_FACE",FACE,{"disambiguationData":[OSD([sQuery(id+"F40.wireOp",EDGE,"E72.left")])]});
            var sketch = newSketch(context, id + "F42", { "sketchPlane" : qUnion([Q0])});
            skCircle(sketch, "E74", {"center": v(0, 144) * mm, "radius": 52.5 * mm});
            skPoint(sketch, "E74.centerSnap0", {"position": v(0, 175) * mm});
            skSolve(sketch);
        }
        {
            var Q0;
            {var subQ0=sQuery(id+"F30.wireOp",EDGE,"E52.top");var subQ1=sQuery(id+"F30.wireOp",EDGE,"E52.bottom");var subQ2=sQuery(id+"F30.wireOp",EDGE,"E51.right");var subQ3=sQuery(id+"F30.wireOp",EDGE,"E52.right");var subQ4=sQuery(id+"F30.wireOp",EDGE,"E51.bottom");var subQ5=sQuery(id+"F30.wireOp",EDGE,"E50.bottom");var subQ6=sQuery(id+"F30.wireOp",EDGE,"E49.bottom");var subQ7=sQuery(id+"F30.wireOp",EDGE,"E54.bottom");var subQ8=sQuery(id+"F30.wireOp",EDGE,"E50.right");var subQ9=sQuery(id+"F30.wireOp",EDGE,"E50.top");var subQ10=sQuery(id+"F30.wireOp",EDGE,"E54.top");var subQ11=sQuery(id+"F30.wireOp",EDGE,"E51.top");var subQ12=sQuery(id+"F30.wireOp",EDGE,"E54.left");var subQ13=sQuery(id+"F30.wireOp",EDGE,"E54.right");Q0=makeQuery(id+"F39.boolean.opBoolean","SPLIT",FACE,{"disambiguationData":[TD([makeQuery(id+"F31.opExtrude","SWEPT_FACE",FACE,{"disambiguationData":[OSD([subQ8])]})])],"derivedFrom":makeQuery(id+"F31.opExtrude","CAP_FACE",FACE,{"disambiguationData":[OSD([subQ6,sQuery(id+"F30.wireOp",EDGE,"E49.top"),sQuery(id+"F30.wireOp",EDGE,"E49.left"),subQ5,subQ9,sQuery(id+"F30.wireOp",EDGE,"E50.left"),subQ8,subQ4,subQ11,subQ2,subQ1,subQ0,sQuery(id+"F30.wireOp",EDGE,"E52.left"),subQ3,sQuery(id+"F30.wireOp",EDGE,"E53.bottom"),sQuery(id+"F30.wireOp",EDGE,"E53.top"),sQuery(id+"F30.wireOp",EDGE,"E53.left"),sQuery(id+"F30.wireOp",EDGE,"E53.right"),subQ7,subQ10,subQ12,subQ13])],"isStart":true})});}
            var sketch = newSketch(context, id + "F43", { "sketchPlane" : qUnion([Q0])});
            skLineSegment(sketch, "E75", {"start": v(-54.83, 79) * mm, "end": v(-54.83, 56) * mm});
            skLineSegment(sketch, "E76", {"start": v(-54.83, 56) * mm, "end": v(-52.83, 56) * mm});
            skLineSegment(sketch, "E77", {"start": v(-52.83, 56) * mm, "end": v(-52.83, 81) * mm});
            skLineSegment(sketch, "E78", {"start": v(-52.83, 81) * mm, "end": v(-77.83, 81) * mm});
            skLineSegment(sketch, "E79", {"start": v(-77.83, 81) * mm, "end": v(-77.83, 79) * mm});
            skLineSegment(sketch, "E80", {"start": v(-77.83, 79) * mm, "end": v(-54.83, 79) * mm});
            skSolve(sketch);
        }
        {
            var Q0;
            Q0 = qSketchRegion(id + "F43", true);
            extrude(context, id + "F44", {"entities" : qUnion([Q0]), "oppositeDirection" : true, "depth" : 120 * mm, "offsetDistance" : 25 * mm});
        }
        {
            var Q0;
            Q0=makeQuery(id+"F44.opExtrude","SWEPT_FACE",FACE,{"disambiguationData":[OSD([sQuery(id+"F43.wireOp",EDGE,"E78")])]});
            var sketch = newSketch(context, id + "F45", { "sketchPlane" : qUnion([Q0])});
            skLineSegment(sketch, "E81.bottom", {"start": v(-77.83, -148) * mm, "end": v(-60.33, -148) * mm});
            skLineSegment(sketch, "E81.top", {"start": v(-77.83, -143) * mm, "end": v(-60.33, -143) * mm});
            skLineSegment(sketch, "E81.left", {"start": v(-77.83, -148) * mm, "end": v(-77.83, -143) * mm});
            skLineSegment(sketch, "E81.right", {"start": v(-60.33, -148) * mm, "end": v(-60.33, -143) * mm});
            skLineSegment(sketch, "E82.bottom", {"start": v(-77.83, -28) * mm, "end": v(-60.33, -28) * mm});
            skLineSegment(sketch, "E82.top", {"start": v(-77.83, -33) * mm, "end": v(-60.33, -33) * mm});
            skLineSegment(sketch, "E82.left", {"start": v(-77.83, -28) * mm, "end": v(-77.83, -33) * mm});
            skLineSegment(sketch, "E82.right", {"start": v(-60.33, -28) * mm, "end": v(-60.33, -33) * mm});
            skSolve(sketch);
        }
        {
            var Q0;
            Q0 = qSketchRegion(id + "F45", true);
            extrude(context, id + "F46", {"entities" : qUnion([Q0]), "operationType" : NewBodyOperationType.REMOVE, "oppositeDirection" : true, "depth" : 34 * mm, "offsetDistance" : 25 * mm});
        }
        {
            var Q0;
            Q0=makeQuery(id+"F39.boolean.opBoolean","COPY",FACE,{"disambiguationData":[TD([makeQuery(id+"F31.opExtrude","SWEPT_FACE",FACE,{"disambiguationData":[OSD([sQuery(id+"F30.wireOp",EDGE,"E50.top")])]})])],"derivedFrom":makeQuery(id+"F39.opExtrude","SWEPT_FACE",FACE,{"disambiguationData":[OSD([sQuery(id+"F36.wireOp",EDGE,"E62.top")])]})});
            var sketch = newSketch(context, id + "F47", { "sketchPlane" : qUnion([Q0])});
            skLineSegment(sketch, "E83.bottom", {"start": v(-97.33, 29) * mm, "end": v(-62.33, 29) * mm});
            skLineSegment(sketch, "E83.top", {"start": v(-97.33, 118) * mm, "end": v(-62.33, 118) * mm});
            skLineSegment(sketch, "E83.left", {"start": v(-97.33, 29) * mm, "end": v(-97.33, 118) * mm});
            skLineSegment(sketch, "E83.right", {"start": v(-62.33, 29) * mm, "end": v(-62.33, 118) * mm});
            skCircle(sketch, "E84", {"center": v(-79.83, 108) * mm, "radius": 5 * mm});
            skPoint(sketch, "E84.centerSnap0", {"position": v(-79.83, 118) * mm});
            skSolve(sketch);
        }
        {
            var Q0;
            Q0 = qSketchRegion(id + "F47", true);
            extrude(context, id + "F48", {"entities" : qUnion([Q0]), "operationType" : NewBodyOperationType.ADD, "depth" : 10 * mm, "offsetDistance" : 25 * mm});
        }
        {
            var Q0;
            Q0=makeQuery(id+"F41.opExtrude","SWEPT_FACE",FACE,{"disambiguationData":[OSD([sQuery(id+"F40.wireOp",EDGE,"E72.bottom")])]});
            var sketch = newSketch(context, id + "F49", { "sketchPlane" : qUnion([Q0])});
            skLineSegment(sketch, "E85.bottom", {"start": v(-104.83, 133) * mm, "end": v(-54.83, 133) * mm});
            skLineSegment(sketch, "E85.top", {"start": v(-104.83, 83) * mm, "end": v(-54.83, 83) * mm});
            skLineSegment(sketch, "E85.left", {"start": v(-104.83, 133) * mm, "end": v(-104.83, 83) * mm});
            skLineSegment(sketch, "E85.right", {"start": v(-54.83, 133) * mm, "end": v(-54.83, 83) * mm});
            skPoint(sketch, "E85.middle", {"position": v(-79.83, 108) * mm});
            skLineSegment(sketch, "E86.bottom", {"start": v(-57.33, 130.5) * mm, "end": v(-102.33, 130.5) * mm});
            skLineSegment(sketch, "E86.top", {"start": v(-57.33, 85.5) * mm, "end": v(-102.33, 85.5) * mm});
            skLineSegment(sketch, "E86.left", {"start": v(-57.33, 130.5) * mm, "end": v(-57.33, 85.5) * mm});
            skLineSegment(sketch, "E86.right", {"start": v(-102.33, 130.5) * mm, "end": v(-102.33, 85.5) * mm});
            skSolve(sketch);
        }
        {
            var Q0;
            Q0 = qSketchRegion(id + "F49", true);
            extrude(context, id + "F50", {"entities" : qUnion([Q0]), "depth" : 75 * mm, "offsetDistance" : 25 * mm});
        }
        {
            var Q0;
            Q0=makeQuery(id+"F44.opExtrude","SWEPT_FACE",FACE,{"disambiguationData":[OSD([sQuery(id+"F43.wireOp",EDGE,"E77")])]});
            var sketch = newSketch(context, id + "F51", { "sketchPlane" : qUnion([Q0])});
            skCircle(sketch, "E87", {"center": v(-138, 67.5) * mm, "radius": 3.53 * mm});
            skCircle(sketch, "E88", {"center": v(-38, 67.5) * mm, "radius": 3.53 * mm});
            skSolve(sketch);
        }
        {
            var Q0;
            {var subQ2=sQuery(id+"F40.wireOp",EDGE,"E72.left");var subQ11=makeQuery(id+"F41.opExtrude","CAP_EDGE",EDGE,{"disambiguationData":[OSD([subQ2])],"isStart":false});Q0=makeQuery(id+"F42.imprint","IMPRINT",FACE,{"disambiguationData":[TD([[makeQuery(id+"F42.imprint","IMPRINT",EDGE,{"derivedFrom":subQ11}),1.0]])]});}
            var Q1;
            Q1 = qSketchRegion(id + "F51", true);
            extrude(context, id + "F52", {"entities" : qUnion([Q0, Q1]), "operationType" : NewBodyOperationType.REMOVE, "oppositeDirection" : true, "depth" : 25 * mm, "offsetDistance" : 25 * mm});
        }
        {
            var Q0;
            Q0=makeQuery(id+"F50.opExtrude","SWEPT_FACE",FACE,{"disambiguationData":[OSD([sQuery(id+"F49.wireOp",EDGE,"E85.right")])]});
            var sketch = newSketch(context, id + "F53", { "sketchPlane" : qUnion([Q0])});
            skCircle(sketch, "E89", {"center": v(-90, 94.5) * mm, "radius": 3 * mm});
            skCircle(sketch, "E90", {"center": v(-35, 94.5) * mm, "radius": 3 * mm});
            skSolve(sketch);
        }
        {
            var Q0;
            Q0 = qSketchRegion(id + "F53", true);
            extrude(context, id + "F54", {"entities" : qUnion([Q0]), "operationType" : NewBodyOperationType.REMOVE, "oppositeDirection" : true, "depth" : 106.1 * mm, "offsetDistance" : 25 * mm});
        }
        {
            var Q0;
            Q0=makeQuery(id+"F50.opExtrude","CAP_FACE",FACE,{"disambiguationData":[OSD([sQuery(id+"F49.wireOp",EDGE,"E85.bottom"),sQuery(id+"F49.wireOp",EDGE,"E85.top"),sQuery(id+"F49.wireOp",EDGE,"E85.left"),sQuery(id+"F49.wireOp",EDGE,"E85.right"),sQuery(id+"F49.wireOp",EDGE,"E86.bottom"),sQuery(id+"F49.wireOp",EDGE,"E86.top"),sQuery(id+"F49.wireOp",EDGE,"E86.left"),sQuery(id+"F49.wireOp",EDGE,"E86.right")])],"isStart":false});
            var sketch = newSketch(context, id + "F55", { "sketchPlane" : qUnion([Q0])});
            skLineSegment(sketch, "E91", {"start": v(-77.83, 83) * mm, "end": v(-77.83, 81) * mm});
            skLineSegment(sketch, "E92", {"start": v(-77.83, 81) * mm, "end": v(-52.83, 81) * mm});
            skLineSegment(sketch, "E93", {"start": v(-52.83, 81) * mm, "end": v(-52.83, 106) * mm});
            skLineSegment(sketch, "E94", {"start": v(-52.83, 106) * mm, "end": v(-54.83, 106) * mm});
            skLineSegment(sketch, "E95", {"start": v(-54.83, 106) * mm, "end": v(-54.83, 83) * mm});
            skLineSegment(sketch, "E96", {"start": v(-54.83, 83) * mm, "end": v(-77.83, 83) * mm});
            skSolve(sketch);
        }
        {
            var Q0;
            Q0 = qSketchRegion(id + "F55", true);
            extrude(context, id + "F56", {"entities" : qUnion([Q0]), "oppositeDirection" : true, "depth" : 75 * mm, "offsetDistance" : 25 * mm});
        }
        {
            var Q0;
            Q0=makeQuery(id+"F56.opExtrude","SWEPT_FACE",FACE,{"disambiguationData":[OSD([sQuery(id+"F55.wireOp",EDGE,"E93")])]});
            var sketch = newSketch(context, id + "F57", { "sketchPlane" : qUnion([Q0])});
            skCircle(sketch, "E97", {"center": v(-90, 94.5) * mm, "radius": 3.25 * mm});
            skCircle(sketch, "E98", {"center": v(-35, 94.5) * mm, "radius": 3.25 * mm});
            skSolve(sketch);
        }
        {
            var Q0;
            Q0 = qSketchRegion(id + "F57", true);
            extrude(context, id + "F58", {"entities" : qUnion([Q0]), "operationType" : NewBodyOperationType.REMOVE, "oppositeDirection" : true, "depth" : 25 * mm, "offsetDistance" : 25 * mm});
        }
    });
